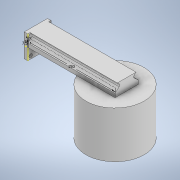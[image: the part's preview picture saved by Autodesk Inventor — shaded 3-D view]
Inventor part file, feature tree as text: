
AUTODESK INVENTOR PART (.ipt)
format: ipt  version: 2021.1 (Build 251245010, 245A)  size: 175,616 bytes
history: native  units: mm
features: sketch x6, extrude x5, plane x4, mirror x2
ambient origin geometry x8: Origin, YZ Plane, XZ Plane, XY Plane, X Axis, Y Axis, Z Axis, Center Point
bodies: Solid1 (feature_tree)
feature tree (17):
  extrude  "Extrusion1"  Depth=40.0mm
  extrude  "Extrusion2"  Depth=6.0mm
  mirror  "Mirror1"
  mirror  "Mirror2"
  plane  "Work Plane4"
  sketch  "Sketch3"  dims[d5=5.0mm d6=6.0mm]
  extrude  "Extrusion3"  Depth=6.0mm
  extrude  "Extrusion4"  [1 undecoded]
  extrude  "Extrusion5"  Depth=150.0mm
  sketch  "Sketch1"  dims[d0=40.0mm d1=40.0mm]
  sketch  "Sketch2"  dims[d2=6.0mm d3=0.0mm d4=5.0mm]
  plane  "Work Plane1"
  plane  "Work Plane2"
  plane  "Work Plane3"
  sketch  "Sketch4"  dims[d7=6.0mm d8=0.0mm d9=-20.0mm]
  sketch  "Sketch5"  dims[d10=15.0mm d11=150.0mm]
  sketch  "Sketch6"  dims[d12=7.5mm d13=150.0mm d14=0.0mm d15=10.0mm d16=60.0mm d17=40.0mm d20=0.0mm d21=93.0mm d22=70.0mm d23=0.0mm]
note: 1 required parameter value undecoded (feature->parameter linkage not recoverable at this tier; creation-order binding heuristic only, values carry confidence <= 0.55)
